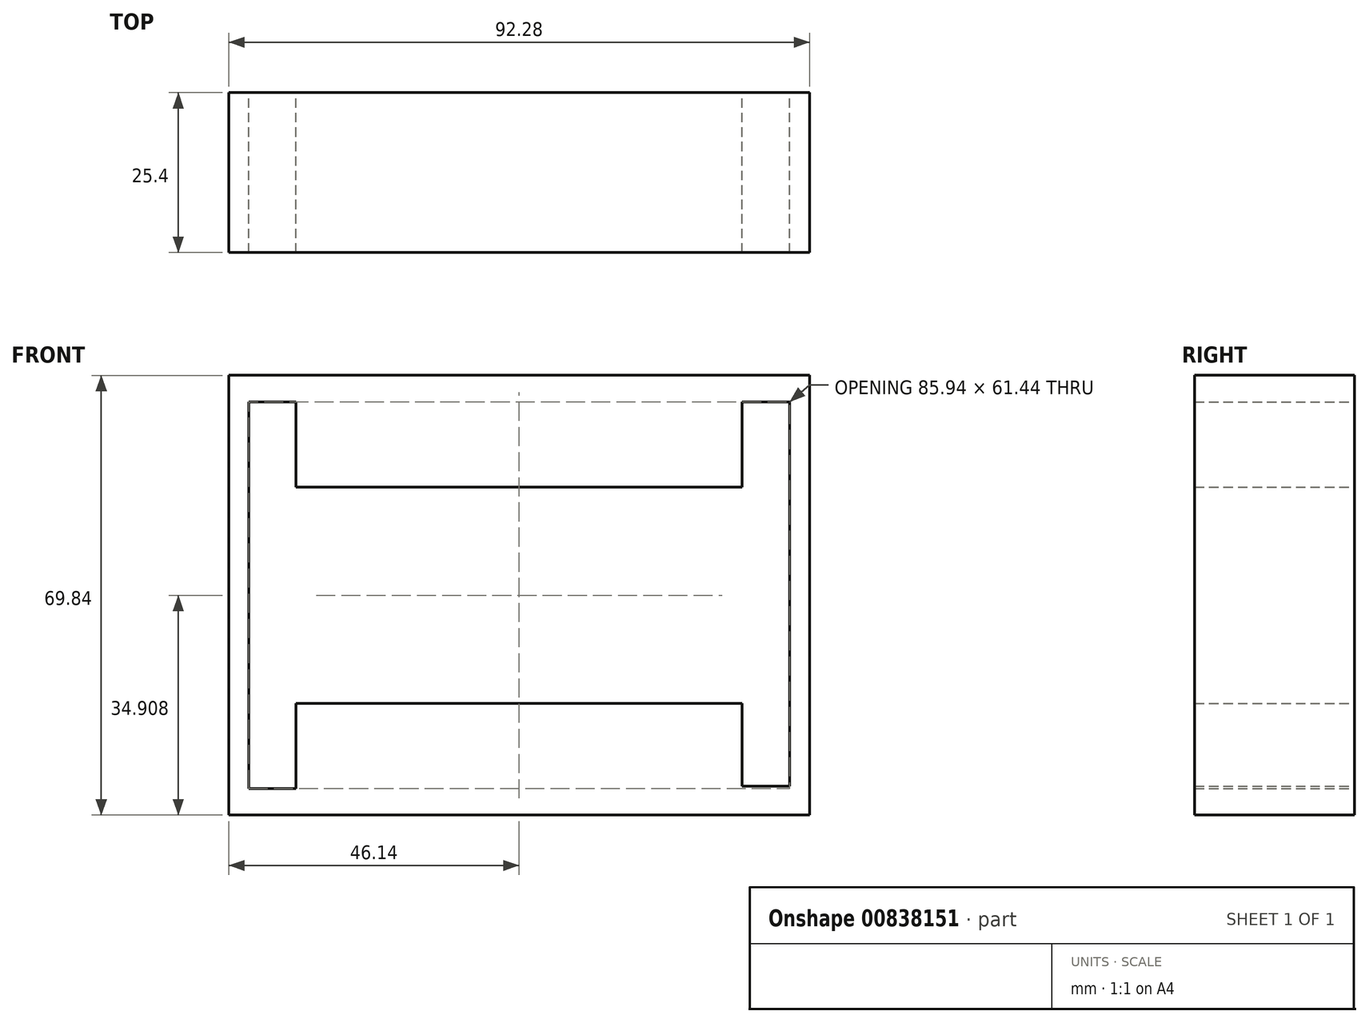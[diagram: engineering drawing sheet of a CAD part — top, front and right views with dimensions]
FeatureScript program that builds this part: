
annotation { "Feature Type Name" : "Feature", "Feature Type Description" : "" }
export const myFeature = defineFeature(function(context is Context, id is Id, definition is map)
    precondition{}
    {
        {
            var Q0;
            Q0=qCreatedBy(makeId("Front.planeOp"),FACE);
            var sketch = newSketch(context, id + "F0", { "sketchPlane" : qUnion([Q0])});
            skLineSegment(sketch, "E0.bottom", {"start": v(-46.14, -34.93) * mm, "end": v(46.14, -34.93) * mm});
            skLineSegment(sketch, "E0.top", {"start": v(-46.14, 34.93) * mm, "end": v(46.14, 34.93) * mm});
            skLineSegment(sketch, "E0.left", {"start": v(-46.14, -34.93) * mm, "end": v(-46.14, 34.93) * mm});
            skLineSegment(sketch, "E0.right", {"start": v(46.14, -34.93) * mm, "end": v(46.14, 34.93) * mm});
            skPoint(sketch, "E0.middle", {"position": v(0, 0) * mm});
            skLineSegment(sketch, "E1.bottom", {"start": v(-46.14, 34.93) * mm, "end": v(-42.97, 34.93) * mm});
            skLineSegment(sketch, "E1.top", {"start": v(-46.14, -34.93) * mm, "end": v(-42.97, -34.93) * mm});
            skLineSegment(sketch, "E1.left", {"start": v(-46.14, 34.93) * mm, "end": v(-46.14, -34.93) * mm});
            skLineSegment(sketch, "E1.right", {"start": v(-42.97, 34.93) * mm, "end": v(-42.97, -34.92) * mm});
            skLineSegment(sketch, "E2.bottom", {"start": v(46.14, -34.93) * mm, "end": v(42.97, -34.93) * mm});
            skLineSegment(sketch, "E2.top", {"start": v(46.14, 34.93) * mm, "end": v(42.97, 34.93) * mm});
            skLineSegment(sketch, "E2.right", {"start": v(42.97, -34.92) * mm, "end": v(42.97, 34.93) * mm});
            skLineSegment(sketch, "E3.bottom", {"start": v(-35.44, 17.18) * mm, "end": v(35.44, 17.18) * mm});
            skLineSegment(sketch, "E3.top", {"start": v(-35.44, -17.18) * mm, "end": v(35.44, -17.18) * mm});
            skLineSegment(sketch, "E3.left", {"start": v(-35.44, 17.18) * mm, "end": v(-35.44, -17.18) * mm});
            skLineSegment(sketch, "E3.right", {"start": v(35.44, 17.18) * mm, "end": v(35.44, -17.18) * mm});
            skLineSegment(sketch, "E4.bottom", {"start": v(-42.97, 34.93) * mm, "end": v(-35.44, 34.93) * mm});
            skLineSegment(sketch, "E4.top", {"start": v(-42.97, -34.93) * mm, "end": v(-35.44, -34.93) * mm});
            skLineSegment(sketch, "E4.left", {"start": v(-42.97, 34.93) * mm, "end": v(-42.97, -34.93) * mm});
            skLineSegment(sketch, "E4.right", {"start": v(-35.44, 34.93) * mm, "end": v(-35.44, -34.93) * mm});
            skPoint(sketch, "E5.oppositeSnap0", {"position": v(35.44, 0) * mm});
            skLineSegment(sketch, "E5.bottom", {"start": v(42.97, 34.93) * mm, "end": v(35.44, 34.93) * mm});
            skLineSegment(sketch, "E5.top", {"start": v(42.97, -34.93) * mm, "end": v(35.44, -34.93) * mm});
            skLineSegment(sketch, "E5.left", {"start": v(42.97, 34.93) * mm, "end": v(42.97, -34.93) * mm});
            skLineSegment(sketch, "E5.right", {"start": v(35.44, 34.93) * mm, "end": v(35.44, -34.93) * mm});
            skLineSegment(sketch, "E6.top", {"start": v(-42.97, 30.7) * mm, "end": v(-35.44, 30.7) * mm});
            skLineSegment(sketch, "E6.left", {"start": v(-42.97, 34.93) * mm, "end": v(-42.97, 30.7) * mm});
            skLineSegment(sketch, "E6.right", {"start": v(-35.44, 34.93) * mm, "end": v(-35.44, 30.7) * mm});
            skLineSegment(sketch, "E7.bottom", {"start": v(35.44, 34.93) * mm, "end": v(42.97, 34.93) * mm});
            skLineSegment(sketch, "E7.top", {"start": v(35.44, 30.7) * mm, "end": v(42.97, 30.7) * mm});
            skLineSegment(sketch, "E7.left", {"start": v(35.44, 34.93) * mm, "end": v(35.44, 30.7) * mm});
            skLineSegment(sketch, "E7.right", {"start": v(42.97, 34.93) * mm, "end": v(42.97, 30.7) * mm});
            skLineSegment(sketch, "E8.top", {"start": v(-42.97, -30.73) * mm, "end": v(-35.44, -30.73) * mm});
            skLineSegment(sketch, "E8.left", {"start": v(-42.97, -34.93) * mm, "end": v(-42.97, -30.73) * mm});
            skLineSegment(sketch, "E8.right", {"start": v(-35.44, -34.93) * mm, "end": v(-35.44, -30.73) * mm});
            skLineSegment(sketch, "E9.top", {"start": v(42.97, -30.32) * mm, "end": v(35.44, -30.32) * mm});
            skLineSegment(sketch, "E9.left", {"start": v(42.97, -34.93) * mm, "end": v(42.97, -30.32) * mm});
            skLineSegment(sketch, "E9.right", {"start": v(35.44, -34.93) * mm, "end": v(35.44, -30.32) * mm});
            skSolve(sketch);
        }
        {
            var Q0;
            Q0 = qSketchRegion(id + "F0", true);
            extrude(context, id + "F1", {"entities" : qUnion([Q0]), "depth" : 25.4 * mm, "offsetDistance" : 25.4 * mm});
        }
    });
